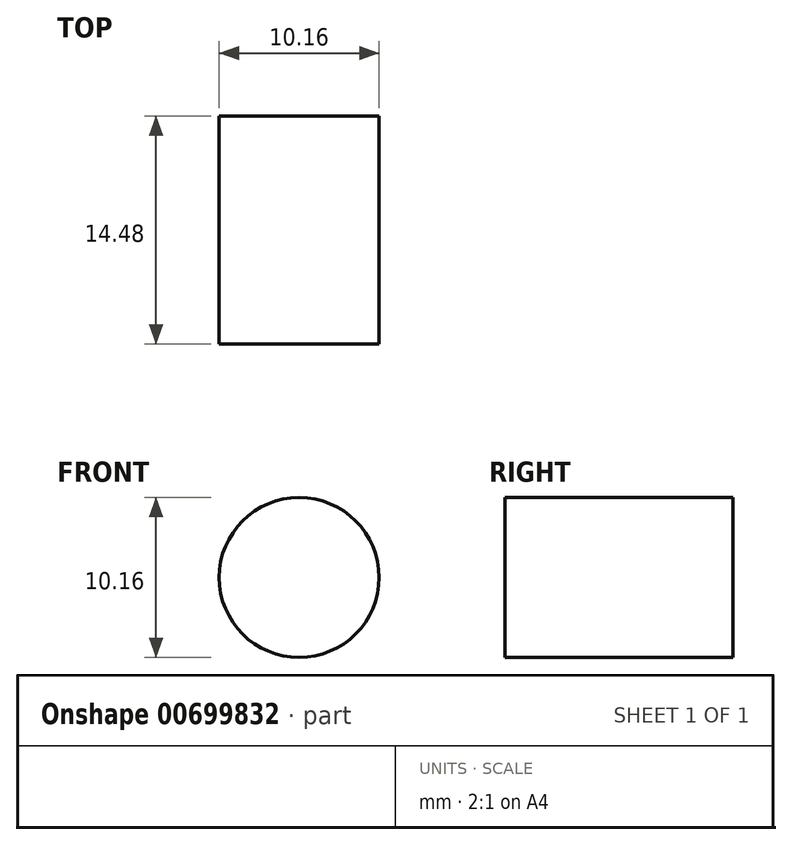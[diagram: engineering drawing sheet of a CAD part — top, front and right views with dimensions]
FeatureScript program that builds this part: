
annotation { "Feature Type Name" : "Feature", "Feature Type Description" : "" }
export const myFeature = defineFeature(function(context is Context, id is Id, definition is map)
    precondition{}
    {
        {
            var Q0;
            Q0=qCreatedBy(makeId("Front.planeOp"),FACE);
            var sketch = newSketch(context, id + "F0", { "sketchPlane" : qUnion([Q0])});
            skCircle(sketch, "E0", {"center": v(0, 0) * mm, "radius": 5.08 * mm});
            skSolve(sketch);
        }
        {
            var Q0;
            Q0=qSketchRegion(id+"F0",true);
            var Q1;
            Q1=makeQuery(id+"F0.imprint","IMPRINT",FACE,{"disambiguationData":[TD([[makeQuery(id+"F0.imprint","IMPRINT",EDGE,{"derivedFrom":sQuery(id+"F0.wireOp",EDGE,"E0")}),1.0]])]});
            extrude(context, id + "F1", {"entities" : qUnion([Q0, Q1]), "depth" : 14.48 * mm});
        }
    });
